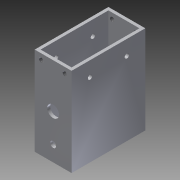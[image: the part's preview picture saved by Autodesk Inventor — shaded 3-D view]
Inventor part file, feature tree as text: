
AUTODESK INVENTOR PART (.ipt)
format: ipt  version: 2013 (Build 170138000, 138)  size: 176,640 bytes
history: native  units: mm
features: sketch x7, hole x5, thread x4, extrude x2, other x1
ambient origin geometry x1: Origin
feature tree (19):
  other  "ソリッド1"
  extrude  "押し出し1"  Depth=25.0mm
  extrude  "押し出し2"  Depth=50.0mm
  hole  "穴1"  [1 undecoded]
  hole  "穴2"  [1 undecoded]
  hole  "穴4"  [1 undecoded]
  thread  "ねじ1"
  thread  "ねじ2"
  thread  "ねじ3"
  thread  "ねじ4"
  hole  "穴5"  [1 undecoded]
  hole  "穴6"  [1 undecoded]
  sketch  "スケッチ1"
  sketch  "スケッチ2"
  sketch  "スケッチ3"
  sketch  "スケッチ4"
  sketch  "スケッチ5"
  sketch  "スケッチ7"
  sketch  "スケッチ8"
note: 5 required parameter values undecoded (feature->parameter linkage not recoverable at this tier; creation-order binding heuristic only, values carry confidence <= 0.55)
